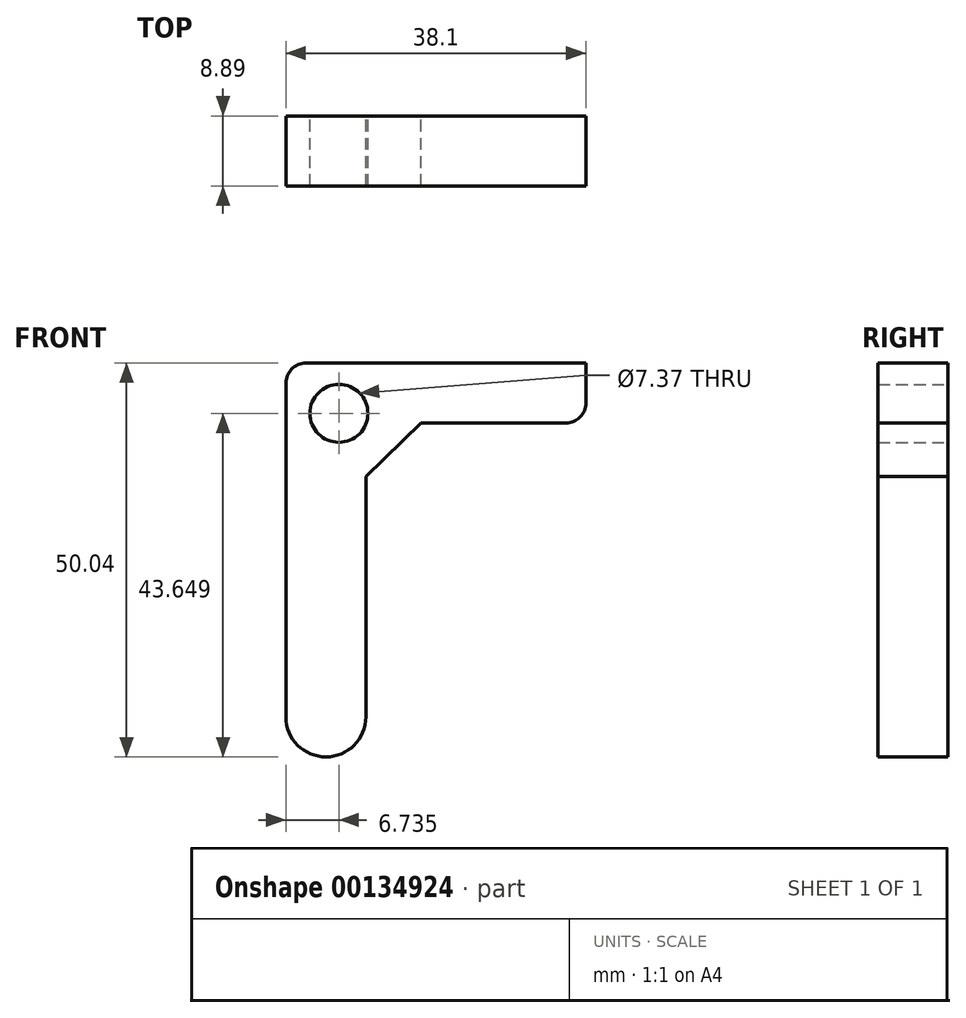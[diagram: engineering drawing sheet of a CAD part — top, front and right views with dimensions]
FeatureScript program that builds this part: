
annotation { "Feature Type Name" : "Feature", "Feature Type Description" : "" }
export const myFeature = defineFeature(function(context is Context, id is Id, definition is map)
    precondition{}
    {
        {
            var Q0;
            Q0=qCreatedBy(makeId("Front.planeOp"),FACE);
            var sketch = newSketch(context, id + "F0", { "sketchPlane" : qUnion([Q0])});
            skLineSegment(sketch, "E0", {"start": v(0, 0) * mm, "end": v(0, 50.8) * mm});
            skLineSegment(sketch, "E1", {"start": v(0, 50.8) * mm, "end": v(38.1, 50.8) * mm});
            skLineSegment(sketch, "E2", {"start": v(38.1, 50.8) * mm, "end": v(38.1, 43.18) * mm});
            skLineSegment(sketch, "E3", {"start": v(38.1, 43.18) * mm, "end": v(10.16, 43.18) * mm});
            skLineSegment(sketch, "E4", {"start": v(10.16, 43.18) * mm, "end": v(10.16, 0) * mm});
            skLineSegment(sketch, "E5", {"start": v(10.16, 0) * mm, "end": v(0, 0) * mm});
            skLineSegment(sketch, "E6", {"start": v(10.16, 36.4) * mm, "end": v(17.14, 43.18) * mm});
            skSolve(sketch);
        }
        {
            var Q0;
            Q0 = qSketchRegion(id + "F0", true);
            extrude(context, id + "F1", {"entities" : qUnion([Q0]), "depth" : 8.9 * mm});
        }
        {
            var Q0;
            Q0=qCreatedBy(makeId("Front.planeOp"),FACE);
            var sketch = newSketch(context, id + "F2", { "sketchPlane" : qUnion([Q0])});
            skCircle(sketch, "E7", {"center": v(6.74, 44.4) * mm, "radius": 3.68 * mm});
            skSolve(sketch);
        }
        {
            var Q0;
            Q0 = qSketchRegion(id + "F2", true);
            extrude(context, id + "F3", {"entities" : qUnion([Q0]), "operationType" : NewBodyOperationType.REMOVE, "depth" : 13.2 * mm});
        }
        {
            var Q0;
            Q0=makeQuery(id+"F1.opExtrude","SWEPT_EDGE",EDGE,{"disambiguationData":[OSD([sQuery(id+"F0.wireOp",EDGE,"E0"),sQuery(id+"F0.wireOp",EDGE,"E1")])]});
            var Q1;
            Q1=makeQuery(id+"F1.opExtrude","SWEPT_EDGE",EDGE,{"disambiguationData":[OSD([sQuery(id+"F0.wireOp",EDGE,"E2"),sQuery(id+"F0.wireOp",EDGE,"E3")])]});
            fillet(context, id + "F4", {"entities" : qUnion([Q0, Q1]), "radius" : 2.54 * mm, "tangentPropagation" : true, "allowEdgeOverflow" : false});
        }
        {
            var Q0;
            Q0=makeQuery(id+"F1.opExtrude","SWEPT_EDGE",EDGE,{"disambiguationData":[OSD([sQuery(id+"F0.wireOp",EDGE,"E0"),sQuery(id+"F0.wireOp",EDGE,"E5")])]});
            var Q1;
            Q1=makeQuery(id+"F1.opExtrude","SWEPT_EDGE",EDGE,{"disambiguationData":[OSD([sQuery(id+"F0.wireOp",EDGE,"E4"),sQuery(id+"F0.wireOp",EDGE,"E5")])]});
            fillet(context, id + "F5", {"entities" : qUnion([Q0, Q1]), "radius" : 5.84 * mm, "tangentPropagation" : true, "allowEdgeOverflow" : false});
        }
        {
            var Q0;
            {var subQ0=sQuery(id+"F0.wireOp",EDGE,"E5");Q0=makeQuery(id+"F5.opFillet","BLEND_EDGE",EDGE,{"blendedFrom":[makeQuery(id+"F1.opExtrude","SWEPT_EDGE",EDGE,{"disambiguationData":[OSD([sQuery(id+"F0.wireOp",EDGE,"E0"),subQ0])]}),makeQuery(id+"F1.opExtrude","SWEPT_EDGE",EDGE,{"disambiguationData":[OSD([sQuery(id+"F0.wireOp",EDGE,"E4"),subQ0])]})],"blendedInto":[]});}
            fillet(context, id + "F6", {"entities" : qUnion([Q0]), "radius" : 5.08 * mm, "tangentPropagation" : true, "allowEdgeOverflow" : false});
        }
    });
